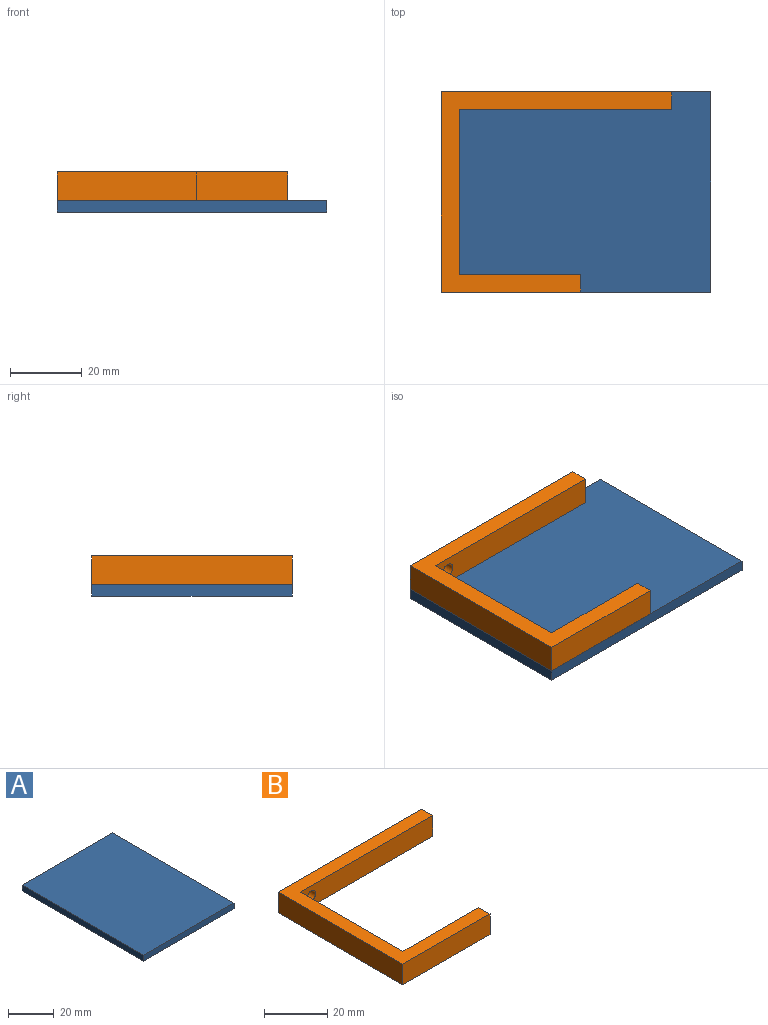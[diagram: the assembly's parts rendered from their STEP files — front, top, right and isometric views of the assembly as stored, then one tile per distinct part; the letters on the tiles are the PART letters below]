
ASSEMBLY  parts=2 mates=1
PART A: 6 faces, bbox 55.8x75x3.2 mm
  f0: plane 75x3.18mm, normal (1,0,0), area 238.1mm2, adj f1,f3,f4,f5
  f1: plane 55.8x3.18mm, normal (0,1,0), area 177.2mm2, adj f0,f2,f4,f5
  f2: plane 75x3.18mm, normal (-1,0,0), area 238.1mm2, adj f1,f3,f4,f5
  f3: plane 55.8x3.18mm, normal (0,-1,0), area 177.2mm2, adj f0,f2,f4,f5
  f4: plane 75x55.8mm, normal (0,0,1), area 4185mm2, adj f0,f1,f2,f3
  f5: plane 75x55.8mm, normal (0,0,-1), area 4185mm2, adj f0,f1,f2,f3
PART B: 11 faces, bbox 64.1x55.8x8 mm
  f0: plane 64.14x8mm, normal (0,1,0), area 500.6mm2, adj f1,f3,f4,f6,f10
  f1: plane 64.14x55.8mm, normal (0,0,-1), area 744.1mm2, adj f0,f2,f5,f6,f7,f8,f9,f10
  f2: plane 59.14x8mm, normal (0,-1,0), area 460.6mm2, adj f1,f3,f4,f5,f10
  f3: plane 64.14x55.8mm, normal (0,0,1), area 744.1mm2, adj f0,f2,f5,f6,f7,f8,f9,f10
  f4: cylinder r=2mm len=5mm, axis (0,1,0), area 62.8mm2, adj f0,f2
  f5: plane 45.8x8mm, normal (1,0,0), area 366.4mm2, adj f1,f2,f3,f9
  f6: plane 55.8x8mm, normal (-1,0,0), area 446.4mm2, adj f0,f1,f3,f7
  f7: plane 38.87x8mm, normal (0,-1,0), area 311mm2, adj f1,f3,f6,f8
  f8: plane 8x5mm, normal (1,0,0), area 40mm2, adj f1,f3,f7,f9
  f9: plane 33.87x8mm, normal (0,1,0), area 271mm2, adj f1,f3,f5,f8
  f10: plane 8x5mm, normal (1,0,0), area 40mm2, adj f0,f1,f2,f3
PLACE A rot(axis=(0,0,-1),90deg) t=(-17.9,44.5,0)mm
PLACE B rot(axis=(1,0,0),0deg) t=(-5.4,72.4,7.17)mm
MATE fastened A.f4 <-> B.f1  axis (0,0,1) through (-55.4,16.6,3.17)mm
